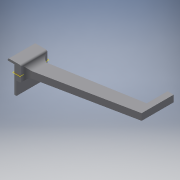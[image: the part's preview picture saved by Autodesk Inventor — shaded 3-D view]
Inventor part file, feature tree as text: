
AUTODESK INVENTOR PART (.ipt)
format: ipt  version: 2018 (Build 220112000, 112)  size: 207,872 bytes
history: native  units: in
note: dims shown in document units (in); Inventor stores cm internally (conversion verified against a paired STEP export)
features: extrude x9, sketch x9, fillet x6, plane x1
ambient origin geometry x8: Origin, YZ Plane, XZ Plane, XY Plane, X Axis, Y Axis, Z Axis, Center Point
bodies: Solid1 (feature_tree)
feature tree (25):
  extrude  "Extrusion1"  Depth=0.6in
  plane  "Work Plane1"
  extrude  "Extrusion2"  Depth=2.0in
  extrude  "Extrusion4"  Depth=0.15in TaperAngle=0.0deg
  extrude  "Extrusion5"  Depth=0.15in TaperAngle=0.0deg
  extrude  "Extrusion6"  Depth=0.3in
  extrude  "Extrusion7"  Depth=0.3in
  extrude  "Extrusion8"  Depth=0.05in TaperAngle=0.0deg
  extrude  "Extrusion9"  Depth=0.125in
  extrude  "Extrusion10"  Depth=0.125in
  fillet  "Fillet4"  Radius=0.125in
  fillet  "Fillet5"  Radius=0.0394in
  fillet  "Fillet6"  [1 undecoded]
  fillet  "Fillet7"  [1 undecoded]
  fillet  "Fillet8"  [1 undecoded]
  fillet  "Fillet9"  [1 undecoded]
  sketch  "Sketch1"  dims[d0=0.3in d1=0.6in]
  sketch  "Sketch2"  dims[d2=0.15in d3=0.0in d4=2.0in]
  sketch  "Sketch4"  dims[d5=0.15in d6=0.0in d9=0.15in d10=0.0in]
  sketch  "Sketch5"  dims[d11=0.15in d12=0.0in d13=0.15in d14=0.0in]
  sketch  "Sketch6"  dims[d15=0.15in d16=0.0in d18=0.3in]
  sketch  "Sketch7"  dims[d19=0.05in d20=0.0in d21=0.3in]
  sketch  "Sketch8"  dims[d22=0.05in d23=0.0in d27=0.05in d28=0.0in]
  sketch  "Sketch9"  dims[d29=0.125in d30=0.125in]
  sketch  "Sketch11"  dims[d31=0.125in d32=0.125in d33=0.125in d34=0.0394in]
note: 4 required parameter values undecoded (feature->parameter linkage not recoverable at this tier; creation-order binding heuristic only, values carry confidence <= 0.55)
